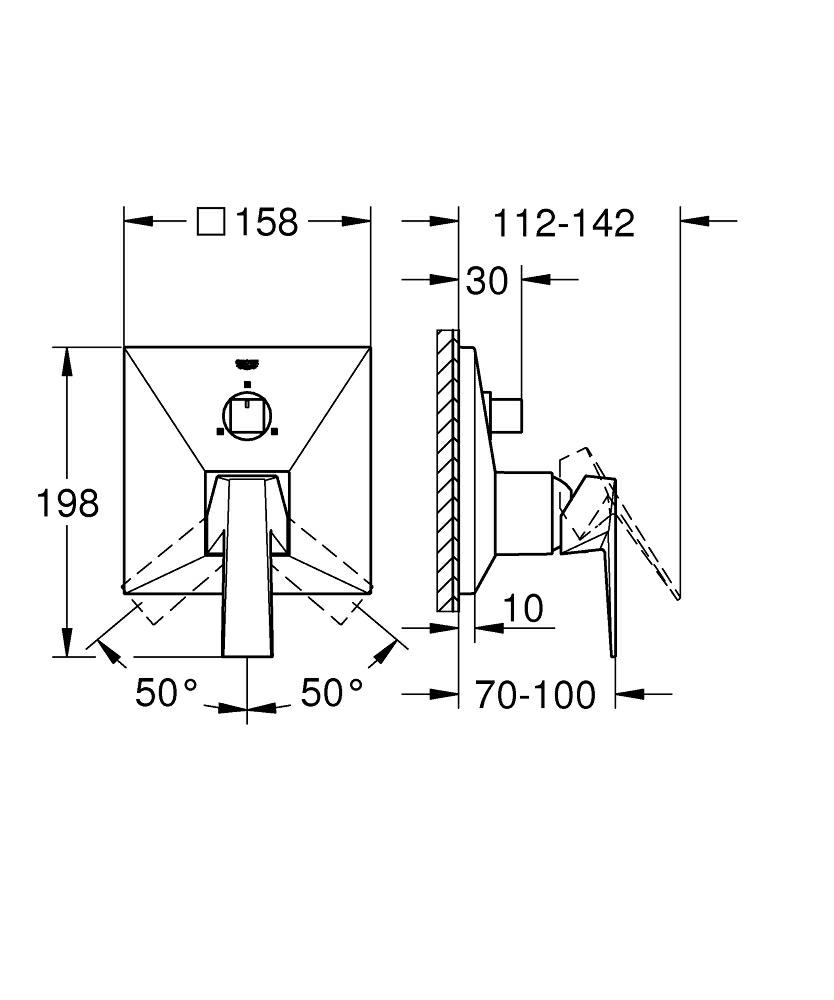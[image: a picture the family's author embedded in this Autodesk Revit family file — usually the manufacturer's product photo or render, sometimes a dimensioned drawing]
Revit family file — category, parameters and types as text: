
# Revit family: Grohe_MixerWithDiverter_AllureBrilliant_24340000
name_source: partatom
category: Plumbing Fixtures
units: mm (PartAtom-declared; Revit-internal decimal feet)

## family parameters
Cut with Voids When Loaded = No
Host = Face
OmniClass Number = 23.45.05.00
OmniClass Title = Sanitary Equipment
Part Type = Normal
Room Calculation Point = No
Round Connector Dimension = Use Diameter
Shared = No

## types (1)
- ALLURE BRILLIANT Single-lever mixer with 3-way diverter (24340000)
    Assembly Code = D2010
    AssetType = Fixed
    BIMObjectName = Grohe_MixerWithDiverter_AllureBrilliant_24340000
    CO2NeutralProduction = GROHE is one of the first leading manufacturer within the sanitary industry having a CO2-neutral production.
    CWFU = 4.5
    ClassificationName = Uniclass2015
    ClassificationValue = Pr_60_75_08_54
    Color = Chrome
    Cost = 0 $
    Default Elevation = 0 mm  [stored 0 ft]
    Description = ALLURE BRILLIANT Single-lever mixer with 3-way diverter
    DocumentationCertificates = https://www.bimstore.co
    DocumentationInstallationGuide = https://www.bimstore.co
    DocumentationLiterature = https://www.bimstore.co
    DocumentationMaintenance = https://www.bimstore.co
    DocumentationTechnical = https://www.bimstore.co
    DurationUnit = Years
    Ecojoy = No
    ExpectedLife = 0
    FullRecyclabilityOfPlastic = All plastic components are fully recycable
    GROHESocialCommittment = green.grohe.com/social_engagement
    GROHESustainability = green.grohe.com
    HWFU = 4.5
    IfcExportAs = IfcPipeFitting
    IfcExportType = IfcPipeFittingType
    Keynote = N13
    Manufacturer = Grohe
    ManufacturerName = Grohe
    Model = ALLURE BRILLIANT Single-lever mixer with 3-way diverter
    ModelNumber = 24340000
    ModelReference = ALLURE BRILLIANT Single-lever mixer with 3-way diverter
    NBSDescription = Mixers
    NBSObjectName = Grohe - Mixers
    NBSReference = 90-70-10/355
    NominalDepth = 0 mm  [stored 0 ft]
    NominalHeight = 0 mm  [stored 0 ft]
    NominalLength = 0 mm  [stored 0 ft]
    PrimaryMaterial = Grohe_Chrome
    ProductNumber = 24340000
    ProductPageURL = https://www.grohe.co.uk
    ProductionYear = 2023
    SustainabilityAward = green.grohe.com/awards
    SustainabilityReport = green.grohe.com/reporting
    Type Comments = ALLURE BRILLIANT Single-lever mixer with 3-way diverter
    TypeName = ALLURE BRILLIANT Single-lever mixer with 3-way diverter
    URL = https://www.grohe.co.uk
    WarrantyDurationLabor = 0
    WarrantyDurationParts = 0
    WarrantyDurationUnit = Years
    _BSBibleVersion = 17
    _BimSpecGuid = 0
    _CurrentRevision = 1
    _DistributedBy = https://www.bimstore.co
    _ObjectUserGuide = https://www.bimstore.co

note: [stored X ft] marks values corroborated as IEEE doubles in the binary element streams (Revit-internal decimal feet)

## geometry (parser evidence)
native form markers: Sweep x2
no freeform markers — native parametric forms only
